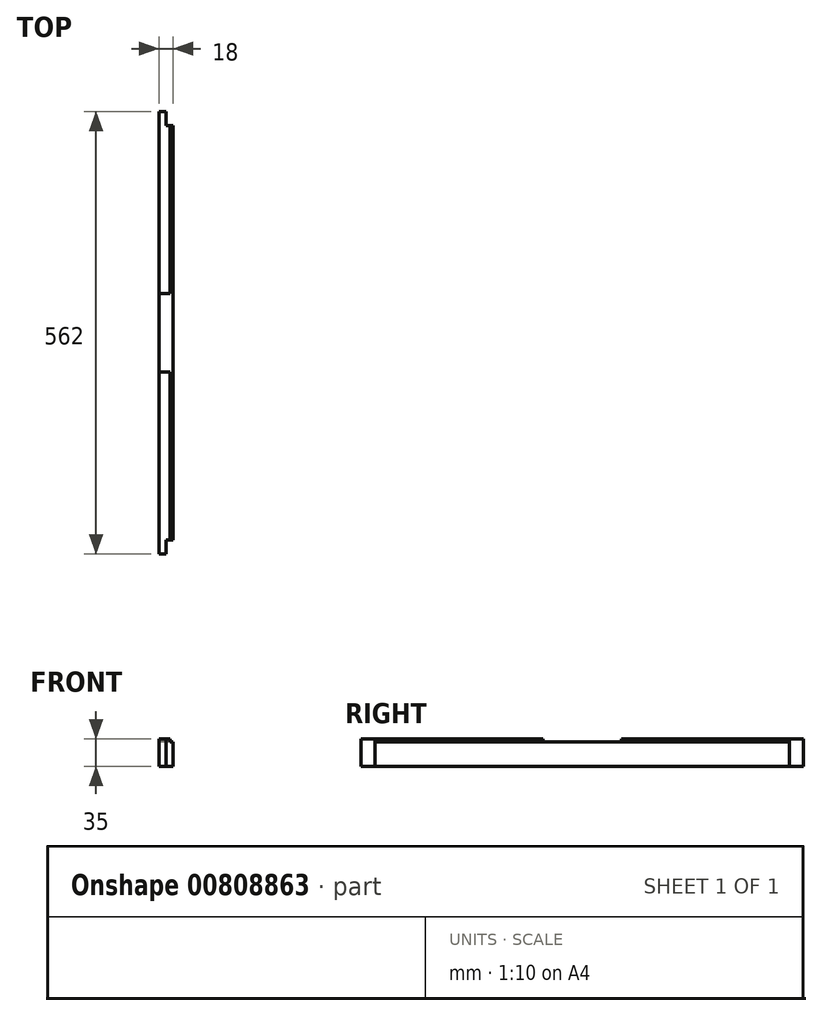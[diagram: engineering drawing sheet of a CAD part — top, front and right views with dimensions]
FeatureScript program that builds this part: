
annotation { "Feature Type Name" : "Feature", "Feature Type Description" : "" }
export const myFeature = defineFeature(function(context is Context, id is Id, definition is map)
    precondition{}
    {
        {
            var Q0;
            Q0=qCreatedBy(makeId("Right.planeOp"),FACE);
            var sketch = newSketch(context, id + "F0", { "sketchPlane" : qUnion([Q0])});
            skLineSegment(sketch, "E0.bottom", {"start": v(0, 0) * mm, "end": v(562, 0) * mm});
            skLineSegment(sketch, "E0.top", {"start": v(0, 35) * mm, "end": v(562, 35) * mm});
            skLineSegment(sketch, "E0.left", {"start": v(0, 0) * mm, "end": v(0, 35) * mm});
            skLineSegment(sketch, "E0.right", {"start": v(562, 0) * mm, "end": v(562, 35) * mm});
            skLineSegment(sketch, "E1.bottom", {"start": v(0, 35) * mm, "end": v(18, 35) * mm});
            skLineSegment(sketch, "E1.top", {"start": v(0, 0) * mm, "end": v(18, 0) * mm});
            skLineSegment(sketch, "E1.left", {"start": v(0, 35) * mm, "end": v(0, 0) * mm});
            skLineSegment(sketch, "E1.right", {"start": v(18, 35) * mm, "end": v(18, 0) * mm});
            skLineSegment(sketch, "E2.bottom", {"start": v(562, 35) * mm, "end": v(544, 35) * mm});
            skLineSegment(sketch, "E2.top", {"start": v(562, 0) * mm, "end": v(544, 0) * mm});
            skLineSegment(sketch, "E2.left", {"start": v(562, 35) * mm, "end": v(562, 0) * mm});
            skLineSegment(sketch, "E2.right", {"start": v(544, 35) * mm, "end": v(544, 0) * mm});
            skLineSegment(sketch, "E3.top", {"start": v(0, 31) * mm, "end": v(562, 31) * mm});
            skLineSegment(sketch, "E3.left", {"start": v(0, 35) * mm, "end": v(0, 31) * mm});
            skLineSegment(sketch, "E3.right", {"start": v(562, 35) * mm, "end": v(562, 31) * mm});
            skLineSegment(sketch, "E4.bottom", {"start": v(281, 35) * mm, "end": v(231, 35) * mm});
            skLineSegment(sketch, "E4.top", {"start": v(281, 31) * mm, "end": v(231, 31) * mm});
            skLineSegment(sketch, "E4.left", {"start": v(281, 35) * mm, "end": v(281, 31) * mm});
            skLineSegment(sketch, "E4.right", {"start": v(231, 35) * mm, "end": v(231, 31) * mm});
            skLineSegment(sketch, "E5.bottom", {"start": v(281, 35) * mm, "end": v(331, 35) * mm});
            skLineSegment(sketch, "E5.top", {"start": v(281, 31) * mm, "end": v(331, 31) * mm});
            skLineSegment(sketch, "E5.right", {"start": v(331, 35) * mm, "end": v(331, 31) * mm});
            skSolve(sketch);
        }
        {
            var Q0;
            {var subQ1=sQuery(id+"F0.wireOp",EDGE,"E1.right");var subQ4=sQuery(id+"F0.wireOp",EDGE,"E0.bottom");var subQ5=makeQuery(id+"F0.imprint","INTERSECT",VERTEX,{"derivedFrom":[subQ4,subQ1]});Q0=makeQuery(id+"F0.imprint","IMPRINT",FACE,{"disambiguationData":[TD([[makeQuery(id+"F0.imprint","IMPRINT",EDGE,{"disambiguationData":[TD([[subQ5,-1.0]])],"derivedFrom":subQ4}),1.0]])]});}
            extrude(context, id + "F1", {"entities" : qUnion([Q0]), "depth" : 18 * mm, "offsetDistance" : 25 * mm});
        }
        {
            var Q0;
            {var subQ0=sQuery(id+"F0.wireOp",EDGE,"E1.right");var subQ1=sQuery(id+"F0.wireOp",EDGE,"E0.bottom");var subQ2=makeQuery(id+"F0.imprint","INTERSECT",VERTEX,{"derivedFrom":[subQ1,subQ0]});Q0=makeQuery(id+"F0.imprint","IMPRINT",FACE,{"disambiguationData":[TD([[makeQuery(id+"F0.imprint","IMPRINT",EDGE,{"disambiguationData":[TD([[subQ2,1.0]])],"derivedFrom":subQ1}),1.0]])]});}
            var Q1;
            {var subQ0=sQuery(id+"F0.wireOp",EDGE,"E0.right");var subQ1=sQuery(id+"F0.wireOp",EDGE,"E0.bottom");var subQ2=makeQuery(id+"F0.imprint","INTERSECT",VERTEX,{"derivedFrom":[subQ1,subQ0]});Q1=makeQuery(id+"F0.imprint","IMPRINT",FACE,{"disambiguationData":[TD([[makeQuery(id+"F0.imprint","IMPRINT",EDGE,{"disambiguationData":[TD([[subQ2,1.0]])],"derivedFrom":subQ1}),1.0]])]});}
            var Q2;
            {var subQ0=sQuery(id+"F0.wireOp",EDGE,"E1.right");var subQ1=sQuery(id+"F0.wireOp",EDGE,"E0.top");var subQ2=makeQuery(id+"F0.imprint","INTERSECT",VERTEX,{"derivedFrom":[subQ1,subQ0]});Q2=makeQuery(id+"F0.imprint","IMPRINT",FACE,{"disambiguationData":[TD([[makeQuery(id+"F0.imprint","IMPRINT",EDGE,{"disambiguationData":[TD([[subQ2,1.0]])],"derivedFrom":subQ1}),-1.0]])]});}
            var Q3;
            {var subQ0=sQuery(id+"F0.wireOp",EDGE,"E0.right");var subQ1=sQuery(id+"F0.wireOp",EDGE,"E0.top");var subQ2=makeQuery(id+"F0.imprint","INTERSECT",VERTEX,{"derivedFrom":[subQ1,subQ0]});Q3=makeQuery(id+"F0.imprint","IMPRINT",FACE,{"disambiguationData":[TD([[makeQuery(id+"F0.imprint","IMPRINT",EDGE,{"disambiguationData":[TD([[subQ2,1.0]])],"derivedFrom":subQ1}),-1.0]])]});}
            extrude(context, id + "F2", {"entities" : qUnion([Q0, Q1, Q2, Q3]), "operationType" : NewBodyOperationType.ADD, "depth" : 9 * mm, "offsetDistance" : 25 * mm});
        }
        {
            var Q0;
            {var subQ3=sQuery(id+"F0.wireOp",EDGE,"E4.right");Q0=makeQuery(id+"F0.imprint","IMPRINT",FACE,{"disambiguationData":[TD([[makeQuery(id+"F0.imprint","IMPRINT",EDGE,{"derivedFrom":subQ3}),-1.0]])]});}
            var Q1;
            {var subQ0=sQuery(id+"F0.wireOp",EDGE,"E5.right");Q1=makeQuery(id+"F0.imprint","IMPRINT",FACE,{"disambiguationData":[TD([[makeQuery(id+"F0.imprint","IMPRINT",EDGE,{"derivedFrom":subQ0}),1.0]])]});}
            extrude(context, id + "F3", {"entities" : qUnion([Q0, Q1]), "operationType" : NewBodyOperationType.ADD, "depth" : 14 * mm, "offsetDistance" : 25 * mm});
        }
    });
